FREECAD ASSEMBLY — COMPONENT RECIPES ("FrontAssembly")

This assembly document has 17 components, labeled P0..P16 below (a component is one placed body or linked part). 9 of them carry a construction recipe — the FreeCAD feature program that regenerates the part from scratch, quoted from this document or its linked companion documents; the rest are supplied as boundary geometry only. No exploded tour is included for this assembly.
COMPONENT P0 — recipe-attached ("FrontCoverPart", a linked part whose construction recipe lives in a companion FreeCAD document of the same project; that document's serialized recipe follows).
Construction recipe (the companion document, serialized — sketch geometry with constraints, then the solid features built on it; lengths are millimeters unless a unit is written):

FCSTD DOCUMENT  (FreeCAD 1.0R39319 (Git))
Label: FrontCover
License: All rights reserved
LicenseURL: https://en.wikipedia.org/wiki/All_rights_reserved
objects: Sketcher::SketchObject×5, PartDesign::Pad×3, PartDesign::SubShapeBinder×2, PartDesign::Pocket×2, PartDesign::Chamfer×1, PartDesign::Body×1, App::Part×1
note: 31 computed .brp shape members not serialized (recipe doc carries the construction recipe); baked Part::Feature solids carry a one-line shape summary decoded from their .brp
EXTERNAL_REF file=../Models/SteeringAckermannModel.FCStd obj=Part
EXTERNAL_REF file=Chassis.FCStd obj=Part

FEATURE [PartDesign::SubShapeBinder] Binder  label="SteeringAckermannModel"
  BindCopyOnChange = 0
  BindMode = 0
  ClaimChildren = false
  Context = -> Part [Body.Binder.]
  Fuse = false
  MakeFace = true
  OffsetFill = false
  OffsetIntersection = false
  OffsetJoinType = 0
  OffsetOpenResult = false
  PartialLoad = false
  Refine = true
  Relative = true
  Support = -> [<external ../Models/SteeringAckermannModel.FCStd>#Part[Sketch001.]]
  _Version = 2
FEATURE [PartDesign::SubShapeBinder] Binder001  label="ChassisSketch002"
  BindCopyOnChange = 0
  BindMode = 0
  ClaimChildren = false
  Context = -> Part [Body.Binder001.]
  Fuse = false
  MakeFace = true
  OffsetFill = false
  OffsetIntersection = false
  OffsetJoinType = 0
  OffsetOpenResult = false
  PartialLoad = false
  Refine = true
  Relative = true
  Support = -> [<external Chassis.FCStd>#Part[Body.Sketch002.]]
  _Version = 2
FEATURE [Sketcher::SketchObject] Sketch
  ArcFitTolerance = 1e-06
  AttachmentSupport = -> [XY_Plane001]
  ExternalGeometry = -> [Binder001,Binder]
  FullyConstrained = true
  MakeInternals = false
  MapMode = 5
  sketch-geometry (27):
    g0: LineSegment StartX=-11.3 StartY=-4 StartZ=0 EndX=-26 EndY=-4 EndZ=0
    g1: LineSegment StartX=-26 StartY=-4 StartZ=0 EndX=-34 EndY=-4 EndZ=0
    g2: LineSegment StartX=-34 StartY=4 StartZ=0 EndX=-26 EndY=4 EndZ=0
    g3: LineSegment StartX=-26 StartY=4 StartZ=0 EndX=-10 EndY=22 EndZ=0
    g4: ArcOfCircle CenterX=-34 CenterY=-2e-16 CenterZ=0 NormalX=0 NormalY=0 NormalZ=1 AngleXU=0 Radius=4 StartAngle=1.5708 EndAngle=4.71239
    g5: LineSegment StartX=11.3 StartY=-4 StartZ=0 EndX=26 EndY=-4 EndZ=0
    g6: LineSegment StartX=26 StartY=4 StartZ=0 EndX=10 EndY=22 EndZ=0
    g7: LineSegment StartX=26 StartY=-4 StartZ=0 EndX=34 EndY=-4 EndZ=0
    g8: LineSegment StartX=26 StartY=4 StartZ=0 EndX=34 EndY=4 EndZ=0
    g9: ArcOfCircle CenterX=34 CenterY=0 CenterZ=0 NormalX=0 NormalY=0 NormalZ=1 AngleXU=0 Radius=4 StartAngle=4.71239 EndAngle=7.85398
    g10: LineSegment StartX=-10 StartY=22 StartZ=0 EndX=10 EndY=22 EndZ=0
    g11: LineSegment StartX=-11.3 StartY=-4 StartZ=0 EndX=-6 EndY=-23.75 EndZ=0
    g12: LineSegment StartX=-6 StartY=-23.75 StartZ=0 EndX=6 EndY=-23.75 EndZ=0
    g13: LineSegment StartX=6 StartY=-23.75 StartZ=0 EndX=11.3 EndY=-4 EndZ=0
    g14: LineSegment StartX=-4.35 StartY=0.65 StartZ=0 EndX=-4.35 EndY=-19.75 EndZ=0
    g15: LineSegment StartX=-4.35 StartY=-19.75 StartZ=0 EndX=4.35 EndY=-19.75 EndZ=0
    g16: LineSegment StartX=4.35 StartY=-19.75 StartZ=0 EndX=4.35 EndY=0.65 EndZ=0
    g17: LineSegment StartX=4.35 StartY=0.65 StartZ=0 EndX=-4.35 EndY=0.65 EndZ=0
    g18: GeomPoint X=4e-16 Y=-9.55 Z=0
    g19: Circle CenterX=0 CenterY=2.25 CenterZ=0 NormalX=0 NormalY=0 NormalZ=1 AngleXU=0 Radius=0.86
    g20: Circle CenterX=-7.473e-13 CenterY=-21.35 CenterZ=0 NormalX=0 NormalY=0 NormalZ=1 AngleXU=0 Radius=0.86
    g21: Circle CenterX=-34 CenterY=-2e-16 CenterZ=0 NormalX=0 NormalY=0 NormalZ=1 AngleXU=0 Radius=1.5
    g22: Circle CenterX=34 CenterY=0 CenterZ=0 NormalX=0 NormalY=0 NormalZ=1 AngleXU=0 Radius=1.5
    g23: Circle CenterX=-22 CenterY=0 CenterZ=0 NormalX=0 NormalY=0 NormalZ=1 AngleXU=0 Radius=1.65
    g24: Circle CenterX=-11.3195 CenterY=16 CenterZ=0 NormalX=0 NormalY=0 NormalZ=1 AngleXU=0 Radius=1.65
    g25: Circle CenterX=11.3195 CenterY=16 CenterZ=0 NormalX=0 NormalY=0 NormalZ=1 AngleXU=0 Radius=1.65
    g26: Circle CenterX=22 CenterY=0 CenterZ=0 NormalX=0 NormalY=0 NormalZ=1 AngleXU=0 Radius=1.65
  constraints (58):
    c: Coincident(g0,g-3)
    c: Coincident(g0,g-4)
    c: Coincident(g1,g0)
    c: Coincident(g2,g-7)
    c: Coincident(g3,g2)
    c: Coincident(g3,g-8)
    c: Tangent(g1,g4) = 1.5708
    c: Tangent(g2,g4) = 1.5708
    c: Coincident(g1,g-5)
    c: Horizontal(g2)
    c: Coincident(g5,g-12)
    c: Coincident(g5,g-13)
    c: Coincident(g6,g-16)
    c: Coincident(g6,g-17)
    c: Coincident(g7,g5)
    c: Coincident(g8,g6)
    c: Tangent(g7,g9) = -1.5708
    c: Tangent(g9,g8) = 1.5708
    c: Horizontal(g8)
    c: Coincident(g7,g-14)
    c: Coincident(g10,g3)
    c: Coincident(g10,g6)
    c: Coincident(g11,g0)
    c: Coincident(g12,g11)
    c: Coincident(g13,g12)
    c: Coincident(g13,g5)
    c: Symmetric(g11,g12,g-2)
    c: DistanceX(g12,g12) = 12
    c: Coincident(g14,g15)
    c: Coincident(g15,g16)
    c: Coincident(g16,g17)
    c: Coincident(g17,g14)
    c: Vertical(g14)
    c: Vertical(g16)
    c: Horizontal(g17)
    c: Symmetric(g14,g15,g-2)
    c: DistanceX(g15,g15) = 8.7
    c: DistanceY(g14,g14) = 20.4
    c: Distance(g-21,g17) = 4.65
    c: Distance(g12,g15) = 4
    c: Symmetric(g14,g16,g18)
    c: Diameter(g19) = 1.72
    c: PointOnObject(g19,g-2)
    c: Equal(g19,g20)
    c: Symmetric(g19,g20,g18)
    c: Distance(g19,g17) = 1.6
    c: Coincident(g21,g4)
    c: Equal(g21,g-9)
    c: Coincident(g22,g9)
    c: Equal(g22,g-18)
    c: Coincident(g23,g-10)
    c: Coincident(g24,g-11)
    c: Coincident(g25,g-20)
    c: Coincident(g26,g-19)
    c: Equal(g23,g26)
    c: Equal(g24,g25)
    c: Diameter(g23) = 3.3
    c: Diameter(g24) = 3.3
FEATURE [PartDesign::Pad] Pad
  Direction = (0,0,1)
  Length = 3
  Length2 = 10
  Profile = -> Sketch
  ReferenceAxis = -> Sketch [N_Axis]
  Refine = true
  Suppressed = false
  Type = 0
FEATURE [Sketcher::SketchObject] Sketch001
  ArcFitTolerance = 1e-06
  AttachmentSupport = -> [Pad]
  ExternalGeometry = -> [Sketch]
  FullyConstrained = true
  MakeInternals = false
  MapMode = 5
  Placement = pos=(0,0,3) rot=(0,0,1;0rad)
  sketch-geometry (13):
    g0: LineSegment StartX=-4.35 StartY=-19.75 StartZ=0 EndX=4.35 EndY=-19.75 EndZ=0
    g1: LineSegment StartX=4.35 StartY=-19.75 StartZ=0 EndX=4.35 EndY=0.65 EndZ=0
    g2: LineSegment StartX=4.35 StartY=0.65 StartZ=0 EndX=-4.35 EndY=0.65 EndZ=0
    g3: LineSegment StartX=-4.35 StartY=0.65 StartZ=0 EndX=-4.35 EndY=-19.75 EndZ=0
    g4: Circle CenterX=0 CenterY=-21.35 CenterZ=0 NormalX=0 NormalY=0 NormalZ=1 AngleXU=0 Radius=0.86
    g5: Circle CenterX=0 CenterY=2.25 CenterZ=0 NormalX=0 NormalY=0 NormalZ=1 AngleXU=0 Radius=0.86
    g6: LineSegment StartX=-6 StartY=-23.75 StartZ=0 EndX=6 EndY=-23.75 EndZ=0
    g7: LineSegment [constr] StartX=-9.81063 StartY=-9.55 StartZ=0 EndX=9.81063 EndY=-9.55 EndZ=0
    g8: LineSegment StartX=-6 StartY=-23.75 StartZ=0 EndX=-9.81063 EndY=-9.55 EndZ=0
    g9: LineSegment StartX=6 StartY=-23.75 StartZ=0 EndX=9.81063 EndY=-9.55 EndZ=0
    g10: LineSegment StartX=-6 StartY=4.65 StartZ=0 EndX=-9.81063 EndY=-9.55 EndZ=0
    g11: LineSegment StartX=-6 StartY=4.65 StartZ=0 EndX=6 EndY=4.65 EndZ=0
    g12: LineSegment StartX=6 StartY=4.65 StartZ=0 EndX=9.81063 EndY=-9.55 EndZ=0
  constraints (27):
    c: Coincident(g0,g-10)
    c: Coincident(g0,g-11)
    c: Coincident(g1,g0)
    c: Coincident(g1,g-12)
    c: Coincident(g2,g1)
    c: Coincident(g2,g-12)
    c: Coincident(g3,g2)
    c: Coincident(g3,g0)
    c: Coincident(g4,g-7)
    c: Equal(g4,g-7)
    c: Coincident(g5,g-8)
    c: Equal(g5,g-8)
    c: Coincident(g6,g-5)
    c: Coincident(g6,g-6)
    c: Horizontal(g7)
    c: Symmetric(g7,g7,g-3)
    c: PointOnObject(g7,g-4)
    c: Coincident(g8,g6)
    c: Coincident(g8,g7)
    c: Coincident(g9,g6)
    c: Coincident(g9,g7)
    c: Coincident(g10,g11)
    c: Coincident(g12,g11)
    c: Symmetric(g6,g10,g7)
    c: Symmetric(g6,g11,g7)
    c: Coincident(g10,g7)
    c: Coincident(g12,g7)
FEATURE [PartDesign::Pad] Pad001
  BaseFeature = -> Pad
  Direction = (0,0,1)
  Length = 5.5
  Length2 = 10
  Profile = -> Sketch001
  ReferenceAxis = -> Sketch001 [N_Axis]
  Refine = true
  Suppressed = false
  Type = 0
FEATURE [Sketcher::SketchObject] Sketch002
  ArcFitTolerance = 1e-06
  AttachmentSupport = -> [Pad001]
  ExternalGeometry = -> [Sketch001]
  FullyConstrained = true
  MakeInternals = false
  MapMode = 5
  Placement = pos=(0,0,3) rot=(0,0,1;0rad)
  sketch-geometry (8):
    g0: LineSegment StartX=-12 StartY=6.65 StartZ=0 EndX=-12 EndY=-1.35 EndZ=0
    g1: LineSegment StartX=-12 StartY=-1.35 StartZ=0 EndX=-13.5 EndY=-1.35 EndZ=0
    g2: LineSegment StartX=-13.5 StartY=-1.35 StartZ=0 EndX=-13.5 EndY=9.65 EndZ=0
    g3: LineSegment StartX=-12 StartY=6.65 StartZ=0 EndX=12 EndY=6.65 EndZ=0
    g4: LineSegment StartX=-13.5 StartY=9.65 StartZ=0 EndX=13.5 EndY=9.65 EndZ=0
    g5: LineSegment StartX=12 StartY=6.65 StartZ=0 EndX=12 EndY=-1.35 EndZ=0
    g6: LineSegment StartX=12 StartY=-1.35 StartZ=0 EndX=13.5 EndY=-1.35 EndZ=0
    g7: LineSegment StartX=13.5 StartY=-1.35 StartZ=0 EndX=13.5 EndY=9.65 EndZ=0
  constraints (20):
    c: Vertical(g0)
    c: Coincident(g1,g0)
    c: Horizontal(g1)
    c: Coincident(g2,g1)
    c: Vertical(g2)
    c: Coincident(g3,g0)
    c: Coincident(g4,g2)
    c: Symmetric(g2,g4,g-2)
    c: Symmetric(g0,g3,g-2)
    c: Coincident(g5,g3)
    c: Coincident(g6,g5)
    c: Coincident(g7,g6)
    c: Coincident(g7,g4)
    c: Symmetric(g1,g6,g-2)
    c: Symmetric(g0,g5,g-2)
    c: DistanceX(g1,g1) = 1.5
    c: DistanceY(g0,g0) = 8
    c: Distance(g4,g3) = 3
    c: Distance(g-3,g3) = 2
    c: DistanceX(g4,g4) = 27
FEATURE [PartDesign::Pad] Pad002
  BaseFeature = -> Pad001
  Direction = (0,0,1)
  Length = 36
  Length2 = 10
  Profile = -> Sketch002
  ReferenceAxis = -> Sketch002 [N_Axis]
  Refine = true
  Suppressed = false
  Type = 0
FEATURE [PartDesign::Chamfer] Chamfer
  Angle = 15
  Base = -> Pad002 [Edge107,Edge99]
  BaseFeature = -> Pad002
  ChamferType = 2
  FlipDirection = false
  Refine = true
  Size = 29.85
  Size2 = 1
  SupportTransform = false
  Suppressed = false
  UseAllEdges = false
FEATURE [Sketcher::SketchObject] Sketch003
  ArcFitTolerance = 1e-06
  AttachmentSupport = -> [Chamfer]
  ExternalGeometry = -> [Chamfer]
  FullyConstrained = true
  MakeInternals = false
  MapMode = 5
  Placement = pos=(0,9.65,0) rot=(0,0.707107,0.707107;3.14159rad)
  sketch-geometry (14):
    g0: LineSegment [constr] StartX=-10.25 StartY=6 StartZ=0 EndX=10.25 EndY=6 EndZ=0
    g1: LineSegment [constr] StartX=10.25 StartY=6 StartZ=0 EndX=10.25 EndY=19.5 EndZ=0
    g2: LineSegment [constr] StartX=10.25 StartY=19.5 StartZ=0 EndX=-10.25 EndY=19.5 EndZ=0
    g3: LineSegment [constr] StartX=-10.25 StartY=19.5 StartZ=0 EndX=-10.25 EndY=6 EndZ=0
    g4: GeomPoint [constr] X=0 Y=12.75 Z=0
    g5: Circle CenterX=-10.25 CenterY=6 CenterZ=0 NormalX=0 NormalY=0 NormalZ=1 AngleXU=0 Radius=1.05
    g6: Circle CenterX=-10.25 CenterY=19.5 CenterZ=0 NormalX=0 NormalY=0 NormalZ=1 AngleXU=0 Radius=1.05
    g7: Circle CenterX=10.25 CenterY=6 CenterZ=0 NormalX=0 NormalY=0 NormalZ=1 AngleXU=0 Radius=1.05
    g8: Circle CenterX=10.25 CenterY=19.5 CenterZ=0 NormalX=0 NormalY=0 NormalZ=1 AngleXU=0 Radius=1.05
    g9: LineSegment StartX=-10 StartY=33.5 StartZ=0 EndX=10 EndY=33.5 EndZ=0
    g10: LineSegment StartX=10 StartY=33.5 StartZ=0 EndX=10 EndY=36.5 EndZ=0
    g11: LineSegment StartX=10 StartY=36.5 StartZ=0 EndX=-10 EndY=36.5 EndZ=0
    g12: LineSegment StartX=-10 StartY=36.5 StartZ=0 EndX=-10 EndY=33.5 EndZ=0
    g13: GeomPoint [constr] X=0 Y=35 Z=0
  constraints (34):
    c: Coincident(g0,g1)
    c: Coincident(g1,g2)
    c: Coincident(g2,g3)
    c: Coincident(g3,g0)
    c: Horizontal(g0)
    c: Horizontal(g2)
    c: Vertical(g1)
    c: Vertical(g3)
    c: Symmetric(g2,g0,g4)
    c: PointOnObject(g4,g-2)
    c: Diameter(g5) = 2.1
    c: Coincident(g6,g2)
    c: Coincident(g7,g0)
    c: Coincident(g8,g1)
    c: Equal(g5,g6)
    c: Equal(g5,g7)
    c: Equal(g6,g8)
    c: DistanceX(g0,g0) = 20.5
    c: DistanceY(g3,g3) = 13.5
    c: Distance(g0,g-3) = 3
    c: Coincident(g5,g0)
    c: Coincident(g9,g10)
    c: Coincident(g10,g11)
    c: Coincident(g11,g12)
    c: Coincident(g12,g9)
    c: Horizontal(g9)
    c: Horizontal(g11)
    c: Vertical(g10)
    c: Vertical(g12)
    c: Symmetric(g11,g9,g13)
    c: PointOnObject(g13,g-2)
    c: DistanceX(g9,g9) = 20
    c: DistanceY(g12,g12) = 3
    c: DistanceY(g2,g9) = 14
FEATURE [PartDesign::Pocket] Pocket
  BaseFeature = -> Chamfer
  Direction = (0,-1,2e-16)
  Length = 0
  Length2 = 5
  Profile = -> Sketch003
  ReferenceAxis = -> Sketch003 [N_Axis]
  Refine = true
  Suppressed = false
  Type = 3
  UpToFace = -> Chamfer [Face6]
FEATURE [Sketcher::SketchObject] Sketch004
  ArcFitTolerance = 1e-06
  AttachmentSupport = -> [Pocket]
  ExternalGeometry = -> [Binder001,Sketch,Sketch001]
  FullyConstrained = true
  MakeInternals = false
  MapMode = 5
  Placement = pos=(0,0,0) rot=(1,0,0;3.14159rad)
  sketch-geometry (8):
    g0: LineSegment StartX=-8 StartY=2.75 StartZ=0 EndX=-11.3 EndY=4 EndZ=0
    g1: LineSegment StartX=-11.3 StartY=4 StartZ=0 EndX=-6 EndY=23.75 EndZ=0
    g2: LineSegment StartX=-6 StartY=23.75 StartZ=0 EndX=6 EndY=23.75 EndZ=0
    g3: LineSegment StartX=6 StartY=23.75 StartZ=0 EndX=11.3 EndY=4 EndZ=0
    g4: LineSegment StartX=11.3 StartY=4 StartZ=0 EndX=8 EndY=2.75 EndZ=0
    g5: LineSegment StartX=-8 StartY=2.75 StartZ=0 EndX=-6 EndY=-4.65 EndZ=0
    g6: LineSegment StartX=-6 StartY=-4.65 StartZ=0 EndX=6 EndY=-4.65 EndZ=0
    g7: LineSegment StartX=6 StartY=-4.65 StartZ=0 EndX=8 EndY=2.75 EndZ=0
  constraints (16):
    c: Coincident(g0,g-7)
    c: Coincident(g1,g0)
    c: Coincident(g1,g-8)
    c: Coincident(g2,g1)
    c: Coincident(g2,g-9)
    c: Coincident(g3,g2)
    c: Coincident(g3,g-9)
    c: Coincident(g4,g3)
    c: Coincident(g4,g-6)
    c: Coincident(g0,g-4)
    c: Coincident(g5,g0)
    c: Coincident(g5,g-11)
    c: Coincident(g6,g5)
    c: Coincident(g6,g-12)
    c: Coincident(g7,g6)
    c: Coincident(g7,g4)
FEATURE [PartDesign::Pocket] Pocket001
  BaseFeature = -> Pocket
  Direction = (0,0,1)
  Length = 1
  Length2 = 5
  Profile = -> Sketch004
  ReferenceAxis = -> Sketch004 [N_Axis]
  Refine = true
  Suppressed = false
  Type = 0
FEATURE [PartDesign::Body] Body  label="FrontCoverBody"
  AllowCompound = false
  Group = -> [Binder,Binder001,Sketch,Pad,Sketch001,Pad001,Sketch002,Pad002,Chamfer,Sketch003,Pocket,Sketch004,Pocket001]
  Origin = -> Origin001
  Tip = -> Pocket001
FEATURE [App::Part] Part  label="FrontCoverPart"
  Group = -> [Body]
  Origin = -> Origin
COMPONENT P1 — geometry summary ("FrontWheelAxleLeftPart"; no construction recipe available for this part):
  bounding box: 26.1 x 13.0 x 13.0 mm
  tessellated surface: 3,524 triangles
  volume: 1277 mm^3 (29% of its bounding box)
  symmetry: mirror-symmetric across its z mid-plane
COMPONENT P2 — geometry summary ("FrontWheelAxleRightPart"; no construction recipe available for this part):
  bounding box: 26.1 x 13.0 x 13.0 mm
  tessellated surface: 3,524 triangles
  volume: 1277 mm^3 (29% of its bounding box)
  symmetry: mirror-symmetric across its z mid-plane
COMPONENT P3 — geometry summary ("FrontWheelStopperPart"; no construction recipe available for this part):
  bounding box: 26.2 x 24.3 x 6.4 mm
  tessellated surface: 4,056 triangles
  volume: 985 mm^3 (24% of its bounding box)
COMPONENT P4 — geometry summary ("FrontWheelStopperPart001"; no construction recipe available for this part):
  bounding box: 26.2 x 24.3 x 6.4 mm
  tessellated surface: 4,056 triangles
  volume: 985 mm^3 (24% of its bounding box)
COMPONENT P5 — geometry summary ("RpiCameraPart"; no construction recipe available for this part):
  bounding box: 25.0 x 24.0 x 19.2 mm
  tessellated surface: 38,449 triangles
  volume: 2510 mm^3 (22% of its bounding box)
  symmetry: mirror-symmetric across its x mid-plane
COMPONENT P6 — recipe-attached ("S0004mPart", a linked part whose construction recipe lives in a companion FreeCAD document of the same project; that document's serialized recipe follows).
Construction recipe (the companion document, serialized — sketch geometry with constraints, then the solid features built on it; lengths are millimeters unless a unit is written):

FCSTD DOCUMENT  (FreeCAD 1.0R39109 (Git))
Label: S0004m
License: All rights reserved
LicenseURL: https://en.wikipedia.org/wiki/All_rights_reserved
objects: Sketcher::SketchObject×5, PartDesign::Pad×5, PartDesign::Body×1, App::Part×1
note: 26 computed .brp shape members not serialized (recipe doc carries the construction recipe); baked Part::Feature solids carry a one-line shape summary decoded from their .brp

FEATURE [Sketcher::SketchObject] Sketch
  ArcFitTolerance = 1e-06
  AttachmentSupport = -> [XY_Plane001]
  FullyConstrained = true
  MakeInternals = false
  MapMode = 5
  sketch-geometry (5):
    g0: LineSegment StartX=-4.25 StartY=-10.1 StartZ=0 EndX=4.25 EndY=-10.1 EndZ=0
    g1: LineSegment StartX=4.25 StartY=-10.1 StartZ=0 EndX=4.25 EndY=10.1 EndZ=0
    g2: LineSegment StartX=4.25 StartY=10.1 StartZ=0 EndX=-4.25 EndY=10.1 EndZ=0
    g3: LineSegment StartX=-4.25 StartY=10.1 StartZ=0 EndX=-4.25 EndY=-10.1 EndZ=0
    g4: GeomPoint [constr] X=0 Y=0 Z=0
  constraints (12):
    c: Coincident(g0,g1)
    c: Coincident(g1,g2)
    c: Coincident(g2,g3)
    c: Coincident(g3,g0)
    c: Horizontal(g0)
    c: Horizontal(g2)
    c: Vertical(g1)
    c: Vertical(g3)
    c: Symmetric(g2,g0,g4)
    c: Distance(g1,g3) = 8.5
    c: Distance(g0,g2) = 20.2
    c: Coincident(g4,g-1)
FEATURE [PartDesign::Pad] Pad
  Direction = (0,0,1)
  Length = 15.2
  Length2 = 10
  Profile = -> Sketch
  ReferenceAxis = -> Sketch [N_Axis]
  Refine = true
  Suppressed = false
  Type = 0
FEATURE [Sketcher::SketchObject] Sketch001
  ArcFitTolerance = 1e-06
  AttachmentSupport = -> [Pad]
  ExternalGeometry = -> [Pad]
  FullyConstrained = true
  MakeInternals = false
  MapMode = 5
  Placement = pos=(0,0,15.2) rot=(0,0,1;0rad)
  sketch-geometry (10):
    g0: LineSegment StartX=4.25 StartY=10.1 StartZ=0 EndX=4.25 EndY=13.6 EndZ=0
    g1: LineSegment StartX=4.25 StartY=13.6 StartZ=0 EndX=-4.25 EndY=13.6 EndZ=0
    g2: LineSegment StartX=-4.25 StartY=13.6 StartZ=0 EndX=-4.25 EndY=10.1 EndZ=0
    g3: LineSegment StartX=-4.25 StartY=-10.1 StartZ=0 EndX=-4.25 EndY=-13.6 EndZ=0
    g4: LineSegment StartX=-4.25 StartY=-13.6 StartZ=0 EndX=4.25 EndY=-13.6 EndZ=0
    g5: LineSegment StartX=4.25 StartY=-13.6 StartZ=0 EndX=4.25 EndY=-10.1 EndZ=0
    g6: Circle CenterX=0 CenterY=11.8 CenterZ=0 NormalX=0 NormalY=0 NormalZ=1 AngleXU=0 Radius=1
    g7: Circle CenterX=0 CenterY=-11.8 CenterZ=0 NormalX=0 NormalY=0 NormalZ=1 AngleXU=0 Radius=1
    g8: LineSegment StartX=-4.25 StartY=10.1 StartZ=0 EndX=-4.25 EndY=-10.1 EndZ=0
    g9: LineSegment StartX=4.25 StartY=-10.1 StartZ=0 EndX=4.25 EndY=10.1 EndZ=0
  constraints (25):
    c: Coincident(g0,g1)
    c: Coincident(g1,g2)
    c: Horizontal(g1)
    c: Vertical(g0)
    c: Vertical(g2)
    c: Coincident(g2,g-3)
    c: Coincident(g0,g-4)
    c: Coincident(g3,g4)
    c: Coincident(g4,g5)
    c: Vertical(g3)
    c: Vertical(g5)
    c: Horizontal(g4)
    c: Coincident(g-3,g3)
    c: Coincident(g-4,g5)
    c: Equal(g2,g3)
    c: DistanceY(g2,g2) = 3.5
    c: PointOnObject(g6,g-2)
    c: Diameter(g6) = 2
    c: Equal(g6,g7)
    c: Symmetric(g6,g7,g-1)
    c: DistanceY(g2,g6) = 1.7
    c: Coincident(g8,g2)
    c: Coincident(g8,g3)
    c: Coincident(g9,g5)
    c: Coincident(g9,g0)
FEATURE [PartDesign::Pad] Pad001
  BaseFeature = -> Pad
  Direction = (0,0,1)
  Length = 0.8
  Length2 = 10
  Profile = -> Sketch001
  ReferenceAxis = -> Sketch001 [N_Axis]
  Refine = true
  Suppressed = false
  Type = 0
FEATURE [Sketcher::SketchObject] Sketch002
  ArcFitTolerance = 1e-06
  AttachmentSupport = -> [Pad001]
  ExternalGeometry = -> [Pad001]
  FullyConstrained = true
  MakeInternals = false
  MapMode = 5
  Placement = pos=(0,0,16) rot=(0,0,1;0rad)
  sketch-geometry (4):
    g0: LineSegment StartX=-4.25 StartY=10.1 StartZ=0 EndX=-4.25 EndY=-10.1 EndZ=0
    g1: LineSegment StartX=-4.25 StartY=-10.1 StartZ=0 EndX=4.25 EndY=-10.1 EndZ=0
    g2: LineSegment StartX=4.25 StartY=-10.1 StartZ=0 EndX=4.25 EndY=10.1 EndZ=0
    g3: LineSegment StartX=4.25 StartY=10.1 StartZ=0 EndX=-4.25 EndY=10.1 EndZ=0
  constraints (10):
    c: Coincident(g0,g1)
    c: Coincident(g1,g2)
    c: Coincident(g2,g3)
    c: Coincident(g3,g0)
    c: Vertical(g0)
    c: Vertical(g2)
    c: Horizontal(g1)
    c: Horizontal(g3)
    c: Coincident(g0,g-6)
    c: Coincident(g1,g-5)
FEATURE [PartDesign::Pad] Pad002
  BaseFeature = -> Pad001
  Direction = (0,0,1)
  Length = 3.5
  Length2 = 10
  Profile = -> Sketch002
  ReferenceAxis = -> Sketch002 [N_Axis]
  Refine = true
  Suppressed = false
  Type = 0
FEATURE [Sketcher::SketchObject] Sketch003
  ArcFitTolerance = 1e-06
  AttachmentSupport = -> [Pad002]
  ExternalGeometry = -> [Pad002]
  FullyConstrained = true
  MakeInternals = false
  MapMode = 5
  Placement = pos=(0,0,19.5) rot=(0,0,1;0rad)
  sketch-geometry (1):
    g0: Circle CenterX=0 CenterY=-5.55 CenterZ=0 NormalX=0 NormalY=0 NormalZ=1 AngleXU=0 Radius=4.25
  constraints (3):
    c: Diameter(g0) = 8.5
    c: PointOnObject(g0,g-2)
    c: Distance(g0,g-3) = 4.55
FEATURE [PartDesign::Pad] Pad003
  BaseFeature = -> Pad002
  Direction = (0,0,1)
  Length = 4.5
  Length2 = 10
  Profile = -> Sketch003
  ReferenceAxis = -> Sketch003 [N_Axis]
  Refine = true
  Suppressed = false
  Type = 0
FEATURE [Sketcher::SketchObject] Sketch004
  ArcFitTolerance = 1e-06
  AttachmentSupport = -> [Pad003]
  ExternalGeometry = -> [Pad003]
  FullyConstrained = true
  MakeInternals = false
  MapMode = 5
  Placement = pos=(0,0,24) rot=(0,0,1;0rad)
  sketch-geometry (1):
    g0: Circle CenterX=0 CenterY=-5.55 CenterZ=0 NormalX=0 NormalY=0 NormalZ=1 AngleXU=0 Radius=1.85
  constraints (2):
    c: Diameter(g0) = 3.7
    c: Coincident(g0,g-3)
FEATURE [PartDesign::Pad] Pad004
  BaseFeature = -> Pad003
  Direction = (0,0,1)
  Length = 2.5
  Length2 = 10
  Profile = -> Sketch004
  ReferenceAxis = -> Sketch004 [N_Axis]
  Refine = true
  Suppressed = false
  Type = 0
FEATURE [PartDesign::Body] Body  label="S0004mBody"
  AllowCompound = false
  Group = -> [Sketch,Pad,Sketch001,Pad001,Sketch002,Pad002,Sketch003,Pad003,Sketch004,Pad004]
  Origin = -> Origin001
  Tip = -> Pad004
FEATURE [App::Part] Part  label="S0004mPart"
  Group = -> [Body]
  Origin = -> Origin
COMPONENT P7 — recipe-attached ("TBoneLinkageBottomPart", a linked part whose construction recipe lives in a companion FreeCAD document of the same project; that document's serialized recipe follows).
Construction recipe (the companion document, serialized — sketch geometry with constraints, then the solid features built on it; lengths are millimeters unless a unit is written):

FCSTD DOCUMENT  (FreeCAD 1.0R39285 (Git))
Label: TBoneLinkageBottom
License: All rights reserved
LicenseURL: https://en.wikipedia.org/wiki/All_rights_reserved
objects: Sketcher::SketchObject×5, PartDesign::Pad×4, App::Link×1, PartDesign::Pocket×1, PartDesign::Body×1, App::Part×1
note: 26 computed .brp shape members not serialized (recipe doc carries the construction recipe); baked Part::Feature solids carry a one-line shape summary decoded from their .brp
EXTERNAL_REF file=../../Models/SteeringAckermannModel.FCStd obj=Spreadsheet

FEATURE [App::Link] Link  label="SteeringAckermannSpreadsheet"
  LinkedObject = -> <external ../../Models/SteeringAckermannModel.FCStd>#Spreadsheet
FEATURE [Sketcher::SketchObject] Sketch
  ArcFitTolerance = 1e-06
  AttachmentSupport = -> [XY_Plane001]
  FullyConstrained = true
  MakeInternals = false
  MapMode = 5
  expr: Constraints[4] = <<SteeringAckermannSpreadsheet>>.servolinkagelength
  expr: Constraints[5] = <<SteeringAckermannSpreadsheet>>.servolinkagesep
  sketch-geometry (8):
    g0: LineSegment [constr] StartX=0 StartY=0 StartZ=0 EndX=0 EndY=-12 EndZ=0
    g1: LineSegment [constr] StartX=-5 StartY=-12 StartZ=0 EndX=5 EndY=-12 EndZ=0
    g2: ArcOfCircle CenterX=0 CenterY=0 CenterZ=0 NormalX=0 NormalY=0 NormalZ=1 AngleXU=0 Radius=4.1 StartAngle=0.394791 EndAngle=2.7468
    g3: ArcOfCircle CenterX=-5 CenterY=-12 CenterZ=0 NormalX=0 NormalY=0 NormalZ=1 AngleXU=0 Radius=4.1 StartAngle=2.7468 EndAngle=4.71239
    g4: ArcOfCircle CenterX=5 CenterY=-12 CenterZ=0 NormalX=0 NormalY=0 NormalZ=1 AngleXU=0 Radius=4.1 StartAngle=4.71239 EndAngle=6.67798
    g5: LineSegment StartX=-8.78462 StartY=-10.4231 StartZ=0 EndX=-3.78462 EndY=1.57692 EndZ=0
    g6: LineSegment StartX=3.78462 StartY=1.57692 StartZ=0 EndX=8.78462 EndY=-10.4231 EndZ=0
    g7: LineSegment StartX=5 StartY=-16.1 StartZ=0 EndX=-5 EndY=-16.1 EndZ=0
  constraints (18):
    c: Coincident(g0,g-1)
    c: Vertical(g0)
    c: Symmetric(g1,g1,g0)
    c: Horizontal(g1)
    c: DistanceY(g0,g0) = 12
    c: DistanceX(g1,g1) = 10
    c: Coincident(g2,g0)
    c: Coincident(g3,g1)
    c: Coincident(g4,g1)
    c: Horizontal(g7)
    c: Tangent(g5,g2) = 1.5708
    c: Tangent(g5,g3) = 1.5708
    c: Tangent(g7,g3) = 1.5708
    c: Tangent(g7,g4) = 1.5708
    c: Tangent(g6,g4) = 1.5708
    c: Tangent(g6,g2) = 1.5708
    c: Radius(g2) = 4.1
    c: Radius(g3) = 4.1
FEATURE [PartDesign::Pad] Pad
  Direction = (0,0,1)
  Length = 2
  Length2 = 10
  Profile = -> Sketch
  ReferenceAxis = -> Sketch [N_Axis]
  Refine = true
  Suppressed = false
  Type = 0
FEATURE [Sketcher::SketchObject] Sketch001
  ArcFitTolerance = 1e-06
  AttachmentSupport = -> [Pad]
  ExternalGeometry = -> [Sketch]
  FullyConstrained = true
  MakeInternals = false
  MapMode = 5
  Placement = pos=(0,0,2) rot=(0,0,1;0rad)
  sketch-geometry (2):
    g0: Circle CenterX=-5 CenterY=-12 CenterZ=0 NormalX=0 NormalY=0 NormalZ=1 AngleXU=0 Radius=2.5
    g1: Circle CenterX=5 CenterY=-12 CenterZ=0 NormalX=0 NormalY=0 NormalZ=1 AngleXU=0 Radius=2.5
  constraints (4):
    c: Coincident(g0,g-3)
    c: Coincident(g1,g-4)
    c: Diameter(g0) = 5
    c: Equal(g0,g1)
FEATURE [PartDesign::Pad] Pad001
  BaseFeature = -> Pad
  Direction = (0,0,1)
  Length = 0.5
  Length2 = 10
  Profile = -> Sketch001
  ReferenceAxis = -> Sketch001 [N_Axis]
  Refine = true
  Suppressed = false
  Type = 0
FEATURE [Sketcher::SketchObject] Sketch002
  ArcFitTolerance = 1e-06
  AttachmentSupport = -> [Pad001]
  ExternalGeometry = -> [Sketch]
  FullyConstrained = true
  MakeInternals = false
  MapMode = 5
  Placement = pos=(0,0,2.5) rot=(0,0,1;0rad)
  sketch-geometry (2):
    g0: Circle CenterX=-5 CenterY=-12 CenterZ=0 NormalX=0 NormalY=0 NormalZ=1 AngleXU=0 Radius=1.5
    g1: Circle CenterX=5 CenterY=-12 CenterZ=0 NormalX=0 NormalY=0 NormalZ=1 AngleXU=0 Radius=1.5
  constraints (4):
    c: Diameter(g0) = 3
    c: Coincident(g0,g-3)
    c: Coincident(g1,g-4)
    c: Equal(g0,g1)
FEATURE [PartDesign::Pad] Pad002
  BaseFeature = -> Pad001
  Direction = (0,0,1)
  Length = 4.5
  Length2 = 10
  Profile = -> Sketch002
  ReferenceAxis = -> Sketch002 [N_Axis]
  Refine = true
  Suppressed = false
  Type = 0
FEATURE [Sketcher::SketchObject] Sketch003
  ArcFitTolerance = 1e-06
  AttachmentSupport = -> [Pad002]
  ExternalGeometry = -> [Sketch]
  FullyConstrained = true
  MakeInternals = false
  MapMode = 5
  Placement = pos=(0,0,2) rot=(0,0,1;0rad)
  sketch-geometry (6):
    g0: ArcOfCircle CenterX=0 CenterY=0 CenterZ=0 NormalX=0 NormalY=0 NormalZ=1 AngleXU=0 Radius=4.1 StartAngle=0.394791 EndAngle=2.7468
    g1: LineSegment StartX=-3.78462 StartY=1.57692 StartZ=0 EndX=-6.47692 EndY=-4.88462 EndZ=0
    g2: LineSegment StartX=3.78462 StartY=1.57692 StartZ=0 EndX=6.47692 EndY=-4.88462 EndZ=0
    g3: LineSegment StartX=-6.47692 StartY=-4.88462 StartZ=0 EndX=-9e-16 EndY=-7.58333 EndZ=0
    g4: LineSegment StartX=-9e-16 StartY=-7.58333 StartZ=0 EndX=6.47692 EndY=-4.88462 EndZ=0
    g5: Circle CenterX=0 CenterY=0 CenterZ=0 NormalX=0 NormalY=0 NormalZ=1 AngleXU=0 Radius=1
  constraints (14):
    c: Coincident(g0,g-1)
    c: Coincident(g3,g1)
    c: Coincident(g4,g2)
    c: Tangent(g1,g0) = -1.5708
    c: Tangent(g2,g0) = 1.5708
    c: Coincident(g0,g-6)
    c: PointOnObject(g2,g-7)
    c: Equal(g1,g2)
    c: Distance(g1,g1) = 7
    c: Perpendicular(g3,g1)
    c: Coincident(g3,g4)
    c: Equal(g3,g4)
    c: Diameter(g5) = 2
    c: Coincident(g5,g0)
FEATURE [PartDesign::Pad] Pad003
  BaseFeature = -> Pad002
  Direction = (0,0,1)
  Length = 3
  Length2 = 10
  Profile = -> Sketch003
  ReferenceAxis = -> Sketch003 [N_Axis]
  Refine = true
  Suppressed = false
  Type = 0
FEATURE [Sketcher::SketchObject] Sketch004
  ArcFitTolerance = 1e-06
  AttachmentSupport = -> [Pad003]
  ExternalGeometry = -> [Sketch]
  FullyConstrained = true
  MakeInternals = false
  MapMode = 5
  Placement = pos=(0,0,0) rot=(1,0,0;3.14159rad)
  sketch-geometry (1):
    g0: Circle CenterX=0 CenterY=0 CenterZ=0 NormalX=0 NormalY=0 NormalZ=1 AngleXU=0 Radius=2.5
  constraints (2):
    c: Diameter(g0) = 5
    c: Coincident(g0,g-1)
FEATURE [PartDesign::Pocket] Pocket
  BaseFeature = -> Pad003
  Direction = (0,0,1)
  Length = 4
  Length2 = 5
  Profile = -> Sketch004
  ReferenceAxis = -> Sketch004 [N_Axis]
  Refine = true
  Suppressed = false
  Type = 0
FEATURE [PartDesign::Body] Body  label="TBoneLinkageBottomBody"
  AllowCompound = false
  Group = -> [Sketch,Pad,Sketch001,Pad001,Sketch002,Pad002,Sketch003,Pad003,Sketch004,Pocket]
  Origin = -> Origin001
  Tip = -> Pocket
FEATURE [App::Part] Part  label="TBoneLinkageBottomPart"
  Group = -> [Body]
  Origin = -> Origin
COMPONENT P8 — recipe-attached ("TBoneLinkageTopPart", a linked part whose construction recipe lives in a companion FreeCAD document of the same project; that document's serialized recipe follows).
Construction recipe (the companion document, serialized — sketch geometry with constraints, then the solid features built on it; lengths are millimeters unless a unit is written):

FCSTD DOCUMENT  (FreeCAD 1.0R39285 (Git))
Label: TBoneLinkageTop
License: All rights reserved
LicenseURL: https://en.wikipedia.org/wiki/All_rights_reserved
objects: Sketcher::SketchObject×2, PartDesign::Pad×2, PartDesign::SubShapeBinder×1, PartDesign::Body×1, App::Part×1
note: 12 computed .brp shape members not serialized (recipe doc carries the construction recipe); baked Part::Feature solids carry a one-line shape summary decoded from their .brp
EXTERNAL_REF file=TBoneLinkageBottom.FCStd obj=Part

FEATURE [PartDesign::SubShapeBinder] Binder  label="TBoneLinkageBottomSketch"
  BindCopyOnChange = 0
  BindMode = 0
  ClaimChildren = false
  Context = -> Part [Body.Binder.]
  Fuse = false
  MakeFace = true
  OffsetFill = false
  OffsetIntersection = false
  OffsetJoinType = 0
  OffsetOpenResult = false
  PartialLoad = false
  Refine = true
  Relative = true
  Support = -> [<external TBoneLinkageBottom.FCStd>#Part[Body.Sketch.]]
  _Version = 2
FEATURE [Sketcher::SketchObject] Sketch
  ArcFitTolerance = 1e-06
  AttachmentSupport = -> [XY_Plane001]
  ExternalGeometry = -> [Binder]
  FullyConstrained = true
  MakeInternals = false
  MapMode = 5
  sketch-geometry (9):
    g0: ArcOfCircle CenterX=0 CenterY=0 CenterZ=0 NormalX=0 NormalY=0 NormalZ=1 AngleXU=0 Radius=4.1 StartAngle=0.394791 EndAngle=2.7468
    g1: ArcOfCircle CenterX=-5 CenterY=-12 CenterZ=0 NormalX=0 NormalY=0 NormalZ=1 AngleXU=0 Radius=4.1 StartAngle=2.7468 EndAngle=4.71239
    g2: ArcOfCircle CenterX=5 CenterY=-12 CenterZ=0 NormalX=0 NormalY=0 NormalZ=1 AngleXU=0 Radius=4.1 StartAngle=4.71239 EndAngle=6.67798
    g3: LineSegment StartX=-3.78462 StartY=1.57692 StartZ=0 EndX=-8.78462 EndY=-10.4231 EndZ=0
    g4: LineSegment StartX=-5.00001 StartY=-16.1 StartZ=0 EndX=5 EndY=-16.1 EndZ=0
    g5: LineSegment StartX=8.78462 StartY=-10.4231 StartZ=0 EndX=3.78462 EndY=1.57692 EndZ=0
    g6: Circle CenterX=-5 CenterY=-12 CenterZ=0 NormalX=0 NormalY=0 NormalZ=1 AngleXU=0 Radius=1.64
    g7: Circle CenterX=5 CenterY=-12 CenterZ=0 NormalX=0 NormalY=0 NormalZ=1 AngleXU=0 Radius=1.64
    g8: Circle CenterX=0 CenterY=0 CenterZ=0 NormalX=0 NormalY=0 NormalZ=1 AngleXU=0 Radius=1.9
  constraints (17):
    c: Coincident(g0,g-1)
    c: Coincident(g1,g-6)
    c: Coincident(g2,g-7)
    c: Coincident(g4,g1)
    c: Tangent(g3,g0) = -1.5708
    c: Tangent(g3,g1) = -1.5708
    c: Tangent(g4,g2) = -1.5708
    c: Tangent(g5,g2) = -1.5708
    c: Tangent(g5,g0) = -1.5708
    c: Coincident(g0,g-5)
    c: Coincident(g2,g-8)
    c: Diameter(g6) = 3.28
    c: Coincident(g6,g1)
    c: Coincident(g7,g2)
    c: Equal(g6,g7)
    c: Diameter(g8) = 3.8
    c: Coincident(g8,g0)
FEATURE [PartDesign::Pad] Pad
  Direction = (0,0,1)
  Length = 2
  Length2 = 10
  Profile = -> Sketch
  ReferenceAxis = -> Sketch [N_Axis]
  Refine = true
  Reversed = true
  Suppressed = false
  Type = 0
FEATURE [Sketcher::SketchObject] Sketch001
  ArcFitTolerance = 1e-06
  AttachmentSupport = -> [Pad]
  ExternalGeometry = -> [Sketch]
  FullyConstrained = true
  MakeInternals = false
  MapMode = 5
  Placement = pos=(0,0,-2) rot=(1,0,0;3.14159rad)
  sketch-geometry (4):
    g0: Circle CenterX=-5 CenterY=12 CenterZ=0 NormalX=0 NormalY=0 NormalZ=1 AngleXU=0 Radius=1.64
    g1: Circle CenterX=5 CenterY=12 CenterZ=0 NormalX=0 NormalY=0 NormalZ=1 AngleXU=0 Radius=1.64
    g2: Circle CenterX=-5 CenterY=12 CenterZ=0 NormalX=0 NormalY=0 NormalZ=1 AngleXU=0 Radius=2.5
    g3: Circle CenterX=5 CenterY=12 CenterZ=0 NormalX=0 NormalY=0 NormalZ=1 AngleXU=0 Radius=2.5
  constraints (8):
    c: Coincident(g0,g-3)
    c: Coincident(g1,g-4)
    c: Equal(g0,g-3)
    c: Equal(g1,g-4)
    c: Coincident(g2,g0)
    c: Coincident(g3,g1)
    c: Diameter(g2) = 5
    c: Equal(g2,g3)
FEATURE [PartDesign::Pad] Pad001
  BaseFeature = -> Pad
  Direction = (0,0,-1)
  Length = 0.5
  Length2 = 10
  Profile = -> Sketch001
  ReferenceAxis = -> Sketch001 [N_Axis]
  Refine = true
  Suppressed = false
  Type = 0
FEATURE [PartDesign::Body] Body  label="TBoneLinkageTopBody"
  AllowCompound = false
  Group = -> [Binder,Sketch,Pad,Sketch001,Pad001]
  Origin = -> Origin001
  Tip = -> Pad001
FEATURE [App::Part] Part  label="TBoneLinkageTopPart"
  Group = -> [Body]
  Origin = -> Origin
COMPONENT P9 — recipe-attached ("TransferLinkageLeftPart", a linked part whose construction recipe lives in a companion FreeCAD document of the same project; that document's serialized recipe follows).
Construction recipe (the companion document, serialized — sketch geometry with constraints, then the solid features built on it; lengths are millimeters unless a unit is written):

FCSTD DOCUMENT  (FreeCAD 1.0R39285 (Git))
Label: TransferLinkageLeft
License: All rights reserved
LicenseURL: https://en.wikipedia.org/wiki/All_rights_reserved
objects: Sketcher::SketchObject×1, App::Link×1, PartDesign::Pad×1, PartDesign::Body×1, App::Part×1
note: 6 computed .brp shape members not serialized (recipe doc carries the construction recipe); baked Part::Feature solids carry a one-line shape summary decoded from their .brp
EXTERNAL_REF file=../../Models/SteeringAckermannModel.FCStd obj=Spreadsheet

FEATURE [Sketcher::SketchObject] Sketch
  ArcFitTolerance = 1e-06
  AttachmentSupport = -> [XY_Plane001]
  FullyConstrained = true
  MakeInternals = false
  MapMode = 5
  expr: Constraints[4] = <<SteeringAckermannSpreadsheet>>.transferlinkagelength
  sketch-geometry (9):
    g0: Circle CenterX=0 CenterY=0 CenterZ=0 NormalX=0 NormalY=0 NormalZ=1 AngleXU=0 Radius=1.66
    g1: Circle CenterX=-32 CenterY=0 CenterZ=0 NormalX=0 NormalY=0 NormalZ=1 AngleXU=0 Radius=1.66
    g2: ArcOfCircle CenterX=0 CenterY=0 CenterZ=0 NormalX=0 NormalY=0 NormalZ=1 AngleXU=0 Radius=2.5 StartAngle=4.71239 EndAngle=7.85398
    g3: LineSegment StartX=8e-16 StartY=2.5 StartZ=0 EndX=-32 EndY=2.5 EndZ=0
    g4: LineSegment StartX=-5e-16 StartY=-2.5 StartZ=0 EndX=-15.88 EndY=-2.5 EndZ=0
    g5: ArcOfCircle CenterX=-32 CenterY=0 CenterZ=0 NormalX=0 NormalY=0 NormalZ=1 AngleXU=0 Radius=2.5 StartAngle=1.5708 EndAngle=5.01328
    g6: LineSegment StartX=-31.2591 StartY=-2.38768 StartZ=0 EndX=-26.1999 EndY=-0.817746 EndZ=0
    g7: ArcOfCircle CenterX=-25.9035 CenterY=-1.77282 CenterZ=0 NormalX=0 NormalY=0 NormalZ=1 AngleXU=0 Radius=1 StartAngle=1.39871 EndAngle=1.87169
    g8: LineSegment StartX=-25.7323 StartY=-0.787589 StartZ=0 EndX=-15.88 EndY=-2.5 EndZ=0
  constraints (21):
    c: Diameter(g0) = 3.32
    c: Coincident(g0,g-1)
    c: Diameter(g1) = 3.32
    c: PointOnObject(g1,g-1)
    c: DistanceX(g1,g0) = 32
    c: Coincident(g2,g0)
    c: Radius(g2) = 2.5
    c: Coincident(g5,g1)
    c: Tangent(g3,g2) = -1.5708
    c: Tangent(g4,g2) = 1.5708
    c: Tangent(g5,g3) = -1.5708
    c: Radius(g5) = 2.5
    c: Distance(g6,g6) = 5.29715
    c: Tangent(g6,g5) = -1.5708
    c: Radius(g7) = 1
    c: Tangent(g7,g6) = 1.5708
    c: Coincident(g8,g4)
    c: Distance(g8,g8) = 10
    c: Tangent(g8,g7) = 1.5708
    c: Parallel(g4,g3)
    c: DistanceX(g4,g4) = 15.88
FEATURE [App::Link] Link  label="SteeringAckermannSpreadsheet"
  LinkedObject = -> <external ../../Models/SteeringAckermannModel.FCStd>#Spreadsheet
FEATURE [PartDesign::Pad] Pad
  Direction = (0,0,1)
  Length = 2
  Length2 = 10
  Profile = -> Sketch
  ReferenceAxis = -> Sketch [N_Axis]
  Refine = true
  Suppressed = false
  Type = 0
FEATURE [PartDesign::Body] Body  label="TransferLinkageLeftBody"
  AllowCompound = false
  Group = -> [Sketch,Pad]
  Origin = -> Origin001
  Tip = -> Pad
FEATURE [App::Part] Part  label="TransferLinkageLeftPart"
  Group = -> [Body]
  Origin = -> Origin
COMPONENT P10 — recipe-attached ("TransferLinkageRightPart", a linked part whose construction recipe lives in a companion FreeCAD document of the same project; that document's serialized recipe follows).
Construction recipe (the companion document, serialized — sketch geometry with constraints, then the solid features built on it; lengths are millimeters unless a unit is written):

FCSTD DOCUMENT  (FreeCAD 1.0R39285 (Git))
Label: TransferLinkageRight
License: All rights reserved
LicenseURL: https://en.wikipedia.org/wiki/All_rights_reserved
objects: PartDesign::SubShapeBinder×1, Part::Mirroring×1, App::Part×1
note: 2 computed .brp shape members not serialized (recipe doc carries the construction recipe); baked Part::Feature solids carry a one-line shape summary decoded from their .brp
EXTERNAL_REF file=TransferLinkageLeft.FCStd obj=Part

FEATURE [PartDesign::SubShapeBinder] Binder  label="TransferLinkageLeftBody"
  BindCopyOnChange = 0
  BindMode = 0
  ClaimChildren = false
  Context = -> Part [Binder.]
  Fuse = false
  MakeFace = true
  OffsetFill = false
  OffsetIntersection = false
  OffsetJoinType = 0
  OffsetOpenResult = false
  PartialLoad = false
  Refine = true
  Relative = true
  Support = -> [<external TransferLinkageLeft.FCStd>#Part[Body.]]
  _Version = 2
FEATURE [Part::Mirroring] Part__Mirroring  label="TransferLinkageRightBody"
  Base = (0,0,0)
  Normal = (1,0,0)
  Source = -> Binder
FEATURE [App::Part] Part  label="TransferLinkageRightPart"
  Group = -> [Binder,Part__Mirroring]
  Origin = -> Origin
COMPONENT P11 — geometry summary ("WheelLinkageBottomLeftPart"; no construction recipe available for this part):
  bounding box: 18.7 x 11.9 x 7.0 mm
  tessellated surface: 2,392 triangles
  volume: 398 mm^3 (26% of its bounding box)
COMPONENT P12 — geometry summary ("WheelLinkageBottomRightPart"; no construction recipe available for this part):
  bounding box: 18.8 x 11.9 x 7.0 mm
  tessellated surface: 2,392 triangles
  volume: 398 mm^3 (25% of its bounding box)
COMPONENT P13 — recipe-attached ("WheelLinkageTopLeftBody", a linked part whose construction recipe lives in a companion FreeCAD document of the same project; that document's serialized recipe follows).
Construction recipe (the companion document, serialized — sketch geometry with constraints, then the solid features built on it; lengths are millimeters unless a unit is written):

FCSTD DOCUMENT  (FreeCAD 1.0R39285 (Git))
Label: WheelLinkageTopLeft
License: All rights reserved
LicenseURL: https://en.wikipedia.org/wiki/All_rights_reserved
objects: PartDesign::SubShapeBinder×3, Sketcher::SketchObject×3, PartDesign::Pad×2, PartDesign::Pocket×2, PartDesign::Body×1, App::Part×1
note: 22 computed .brp shape members not serialized (recipe doc carries the construction recipe); baked Part::Feature solids carry a one-line shape summary decoded from their .brp
EXTERNAL_REF file=WheelLinkageBottomLeft.FCStd obj=Part

FEATURE [PartDesign::SubShapeBinder] Binder  label="WheelLinkageBottomLeftSketch"
  BindCopyOnChange = 0
  BindMode = 0
  ClaimChildren = false
  Context = -> Part [Body.Binder.]
  Fuse = false
  MakeFace = true
  OffsetFill = false
  OffsetIntersection = false
  OffsetJoinType = 0
  OffsetOpenResult = false
  PartialLoad = false
  Refine = true
  Relative = true
  Support = -> [<external WheelLinkageBottomLeft.FCStd>#Part[Body.Sketch.]]
  _Version = 2
FEATURE [PartDesign::Pad] Pad
  Direction = (0,0,1)
  Length = 2
  Length2 = 10
  Profile = -> Binder
  Refine = true
  Reversed = true
  Suppressed = false
  Type = 0
FEATURE [PartDesign::SubShapeBinder] Binder001  label="WheelLinkageBottomLeftSketch003"
  BindCopyOnChange = 0
  BindMode = 0
  ClaimChildren = false
  Context = -> Part [Body.Binder001.]
  Fuse = false
  MakeFace = true
  OffsetFill = false
  OffsetIntersection = false
  OffsetJoinType = 0
  OffsetOpenResult = false
  PartialLoad = false
  Refine = true
  Relative = true
  Support = -> [<external WheelLinkageBottomLeft.FCStd>#Part[Body.Sketch003.]]
  _Version = 2
FEATURE [Sketcher::SketchObject] Sketch
  ArcFitTolerance = 1e-06
  AttachmentSupport = -> [Pad]
  ExternalGeometry = -> [Binder001]
  FullyConstrained = true
  MakeInternals = false
  MapMode = 5
  Placement = pos=(0,0,-2) rot=(1,0,0;3.14159rad)
  sketch-geometry (1):
    g0: Circle CenterX=-5 CenterY=0 CenterZ=0 NormalX=0 NormalY=0 NormalZ=1 AngleXU=0 Radius=1.68
  constraints (2):
    c: Coincident(g0,g-3)
    c: Diameter(g0) = 3.36
FEATURE [PartDesign::Pocket] Pocket
  BaseFeature = -> Pad
  Direction = (0,0,1)
  Length = 0
  Length2 = 5
  Profile = -> Sketch
  ReferenceAxis = -> Sketch [N_Axis]
  Refine = true
  Suppressed = false
  Type = 3
  UpToFace = -> Pad [Face8]
FEATURE [PartDesign::SubShapeBinder] Binder002  label="WheelLinkageBottomLeftSketch002"
  BindCopyOnChange = 0
  BindMode = 0
  ClaimChildren = false
  Context = -> Part [Body.Binder002.]
  Fuse = false
  MakeFace = true
  OffsetFill = false
  OffsetIntersection = false
  OffsetJoinType = 0
  OffsetOpenResult = false
  PartialLoad = false
  Refine = true
  Relative = true
  Support = -> [<external WheelLinkageBottomLeft.FCStd>#Part[Body.Sketch001.]]
  _Version = 2
FEATURE [Sketcher::SketchObject] Sketch001
  ArcFitTolerance = 1e-06
  AttachmentSupport = -> [Pocket]
  ExternalGeometry = -> [Binder002]
  FullyConstrained = true
  MakeInternals = false
  MapMode = 5
  Placement = pos=(0,0,-2) rot=(1,0,0;3.14159rad)
  sketch-geometry (1):
    g0: Circle CenterX=-2.70757 CenterY=11.6906 CenterZ=0 NormalX=0 NormalY=0 NormalZ=1 AngleXU=0 Radius=2.5
  constraints (2):
    c: Coincident(g0,g-3)
    c: Equal(g0,g-3)
FEATURE [PartDesign::Pad] Pad001
  BaseFeature = -> Pocket
  Direction = (0,0,-1)
  Length = 0.5
  Length2 = 10
  Profile = -> Sketch001
  ReferenceAxis = -> Sketch001 [N_Axis]
  Refine = true
  Suppressed = false
  Type = 0
FEATURE [Sketcher::SketchObject] Sketch002
  ArcFitTolerance = 1e-06
  AttachmentSupport = -> [Pad001]
  ExternalGeometry = -> [Sketch001]
  FullyConstrained = true
  MakeInternals = false
  MapMode = 5
  Placement = pos=(0,0,-2.5) rot=(1,0,0;3.14159rad)
  sketch-geometry (1):
    g0: Circle CenterX=-2.70757 CenterY=11.6906 CenterZ=0 NormalX=0 NormalY=0 NormalZ=1 AngleXU=0 Radius=1.64
  constraints (2):
    c: Diameter(g0) = 3.28
    c: Coincident(g0,g-3)
FEATURE [PartDesign::Pocket] Pocket001
  BaseFeature = -> Pad001
  Direction = (0,0,1)
  Length = 0
  Length2 = 5
  Profile = -> Sketch002
  ReferenceAxis = -> Sketch002 [N_Axis]
  Refine = true
  Suppressed = false
  Type = 3
  UpToFace = -> Pad001 [Face4]
FEATURE [PartDesign::Body] Body  label="WheelLinkageTopLeftBody"
  AllowCompound = false
  Group = -> [Binder,Pad,Binder001,Sketch,Pocket,Binder002,Sketch001,Pad001,Sketch002,Pocket001]
  Origin = -> Origin001
  Tip = -> Pocket001
FEATURE [App::Part] Part  label="WheelLinkageTopLeftPart"
  Group = -> [Body]
  Origin = -> Origin
COMPONENT P14 — geometry summary ("WheelLinkageTopRightPart"; no construction recipe available for this part):
  bounding box: 18.8 x 11.9 x 2.5 mm
  tessellated surface: 2,400 triangles
  volume: 292 mm^3 (52% of its bounding box)
COMPONENT P15 — recipe-attached ("WheelPart", a linked part whose construction recipe lives in a companion FreeCAD document of the same project; that document's serialized recipe follows).
Construction recipe (the companion document, serialized — sketch geometry with constraints, then the solid features built on it; lengths are millimeters unless a unit is written):

FCSTD DOCUMENT  (FreeCAD 1.0R39109 (Git))
Label: Wheel
License: All rights reserved
LicenseURL: https://en.wikipedia.org/wiki/All_rights_reserved
objects: Sketcher::SketchObject×5, PartDesign::Pad×4, PartDesign::Pocket×1, PartDesign::Body×1, App::Part×1
note: 26 computed .brp shape members not serialized (recipe doc carries the construction recipe); baked Part::Feature solids carry a one-line shape summary decoded from their .brp

FEATURE [Sketcher::SketchObject] Sketch
  ArcFitTolerance = 1e-06
  AttachmentSupport = -> [YZ_Plane001]
  FullyConstrained = true
  MakeInternals = false
  MapMode = 5
  Placement = pos=(0,0,0) rot=(0.57735,0.57735,0.57735;2.0944rad)
  sketch-geometry (2):
    g0: Circle CenterX=0 CenterY=0 CenterZ=0 NormalX=0 NormalY=0 NormalZ=1 AngleXU=0 Radius=17.5
    g1: Circle CenterX=0 CenterY=0 CenterZ=0 NormalX=0 NormalY=0 NormalZ=1 AngleXU=0 Radius=27.5
  constraints (4):
    c: Diameter(g0) = 35
    c: Coincident(g0,g-1)
    c: Coincident(g1,g0)
    c: Diameter(g1) = 55
FEATURE [PartDesign::Pad] Pad
  Direction = (1,0,0)
  Length = 25
  Length2 = 10
  Placement = pos=(0,0,0) rot=(1,1,1;2.0944rad)
  Profile = -> Sketch
  ReferenceAxis = -> Sketch [N_Axis]
  Refine = true
  Reversed = true
  Suppressed = false
  Type = 0
FEATURE [Sketcher::SketchObject] Sketch001
  ArcFitTolerance = 1e-06
  AttachmentSupport = -> [YZ_Plane001]
  FullyConstrained = true
  MakeInternals = false
  MapMode = 5
  Placement = pos=(0,0,0) rot=(0.57735,0.57735,0.57735;2.0944rad)
  sketch-geometry (9):
    g0: Circle CenterX=0 CenterY=0 CenterZ=0 NormalX=0 NormalY=0 NormalZ=1 AngleXU=0 Radius=17.5
    g1: Circle CenterX=0 CenterY=0 CenterZ=0 NormalX=0 NormalY=0 NormalZ=1 AngleXU=0 Radius=4.55
    g2: LineSegment [constr] StartX=0 StartY=10 StartZ=0 EndX=-8.66025 EndY=-5 EndZ=0
    g3: LineSegment [constr] StartX=-8.66025 StartY=-5 StartZ=0 EndX=8.66025 EndY=-5 EndZ=0
    g4: LineSegment [constr] StartX=8.66025 StartY=-5 StartZ=0 EndX=0 EndY=10 EndZ=0
    g5: Circle [constr] CenterX=0 CenterY=0 CenterZ=0 NormalX=0 NormalY=0 NormalZ=1 AngleXU=0 Radius=10
    g6: Circle CenterX=0 CenterY=10 CenterZ=0 NormalX=0 NormalY=0 NormalZ=1 AngleXU=0 Radius=1.5
    g7: Circle CenterX=-8.66025 CenterY=-5 CenterZ=0 NormalX=0 NormalY=0 NormalZ=1 AngleXU=0 Radius=1.5
    g8: Circle CenterX=8.66025 CenterY=-5 CenterZ=0 NormalX=0 NormalY=0 NormalZ=1 AngleXU=0 Radius=1.5
  constraints (21):
    c: Diameter(g0) = 35
    c: Coincident(g0,g-1)
    c: Diameter(g1) = 9.1
    c: Coincident(g1,g0)
    c: Coincident(g2,g3)
    c: Coincident(g3,g4)
    c: Coincident(g4,g2)
    c: Equal(g2,g3)
    c: Equal(g2,g4)
    c: PointOnObject(g2,g5)
    c: PointOnObject(g3,g5)
    c: PointOnObject(g4,g5)
    c: Coincident(g5,g0)
    c: PointOnObject(g4,g-2)
    c: Diameter(g6) = 3
    c: Coincident(g6,g2)
    c: Diameter(g7) = 3
    c: Coincident(g7,g2)
    c: Diameter(g8) = 3
    c: Coincident(g8,g3)
    c: DistanceY(g0,g2) = 10
FEATURE [PartDesign::Pad] Pad001
  BaseFeature = -> Pad
  Direction = (1,0,0)
  Length = 16
  Length2 = 10
  Placement = pos=(0,0,0) rot=(1,1,1;2.0944rad)
  Profile = -> Sketch001
  ReferenceAxis = -> Sketch001 [N_Axis]
  Refine = true
  Reversed = true
  Suppressed = false
  Type = 0
FEATURE [Sketcher::SketchObject] Sketch002
  ArcFitTolerance = 1e-06
  AttachmentSupport = -> [YZ_Plane001]
  FullyConstrained = true
  MakeInternals = false
  MapMode = 5
  Placement = pos=(0,0,0) rot=(0.57735,0.57735,0.57735;2.0944rad)
  sketch-geometry (1):
    g0: Circle CenterX=0 CenterY=0 CenterZ=0 NormalX=0 NormalY=0 NormalZ=1 AngleXU=0 Radius=17.5
  constraints (2):
    c: Diameter(g0) = 35
    c: Coincident(g0,g-1)
FEATURE [PartDesign::Pocket] Pocket
  BaseFeature = -> Pad001
  Direction = (-1,0,0)
  Length = 13
  Length2 = 5
  Placement = pos=(0,0,0) rot=(1,1,1;2.0944rad)
  Profile = -> Sketch002
  ReferenceAxis = -> Sketch002 [N_Axis]
  Refine = true
  Suppressed = false
  Type = 0
FEATURE [Sketcher::SketchObject] Sketch003
  ArcFitTolerance = 1e-06
  AttachmentSupport = -> [Pocket]
  FullyConstrained = true
  MakeInternals = false
  MapMode = 5
  Placement = pos=(-13,2.9e-15,-1.4e-15) rot=(0.57735,0.57735,0.57735;2.0944rad)
  sketch-geometry (2):
    g0: Circle CenterX=0 CenterY=0 CenterZ=0 NormalX=0 NormalY=0 NormalZ=1 AngleXU=0 Radius=4.55
    g1: Circle CenterX=0 CenterY=0 CenterZ=0 NormalX=0 NormalY=0 NormalZ=1 AngleXU=0 Radius=5.55
  constraints (4):
    c: Diameter(g0) = 9.1
    c: Coincident(g0,g-1)
    c: Coincident(g1,g0)
    c: Diameter(g1) = 11.1
FEATURE [PartDesign::Pad] Pad002
  BaseFeature = -> Pocket
  Direction = (1,0,0)
  Length = 2
  Length2 = 10
  Placement = pos=(0,0,0) rot=(1,1,1;2.0944rad)
  Profile = -> Sketch003
  ReferenceAxis = -> Sketch003 [N_Axis]
  Refine = true
  Suppressed = false
  Type = 0
FEATURE [Sketcher::SketchObject] Sketch004
  ArcFitTolerance = 1e-06
  AttachmentSupport = -> [Pad002]
  FullyConstrained = true
  MakeInternals = false
  MapMode = 5
  Placement = pos=(-16,1.07e-14,-5.3e-15) rot=(0.57735,0.57735,-0.57735;4.18879rad)
  sketch-geometry (2):
    g0: Circle CenterX=0 CenterY=0 CenterZ=0 NormalX=0 NormalY=0 NormalZ=1 AngleXU=0 Radius=4.55
    g1: Circle CenterX=0 CenterY=0 CenterZ=0 NormalX=0 NormalY=0 NormalZ=1 AngleXU=0 Radius=5.55
  constraints (4):
    c: Diameter(g0) = 9.1
    c: Coincident(g0,g-1)
    c: Diameter(g1) = 11.1
    c: Coincident(g1,g0)
FEATURE [PartDesign::Pad] Pad003
  BaseFeature = -> Pad002
  Direction = (-1,0,0)
  Length = 2
  Length2 = 10
  Placement = pos=(0,0,0) rot=(1,1,1;2.0944rad)
  Profile = -> Sketch004
  ReferenceAxis = -> Sketch004 [N_Axis]
  Refine = true
  Suppressed = false
  Type = 0
FEATURE [PartDesign::Body] Body  label="WheelBody"
  AllowCompound = false
  Group = -> [Sketch,Pad,Sketch001,Pad001,Sketch002,Pocket,Sketch003,Pad002,Sketch004,Pad003]
  Origin = -> Origin001
  Tip = -> Pad003
FEATURE [App::Part] Part  label="WheelPart"
  Group = -> [Body]
  Origin = -> Origin
COMPONENT P16 — same part as P15; its construction recipe is shown at P15.
PROVENANCE & LICENSES
A FreeCAD (.FCStd) document from a public repository crawl; recipes are the document's own serialized feature recipes (and, for linked parts, companion documents' recipes).
License: as declared in the source repository (recorded in the dataset sidecar).
